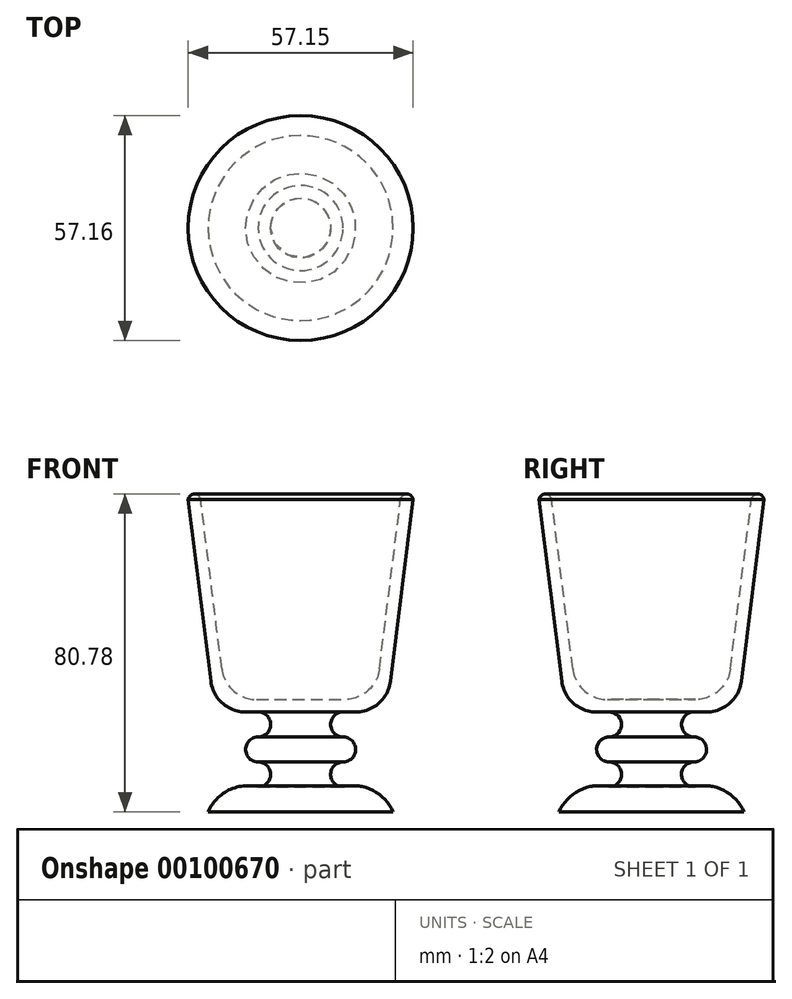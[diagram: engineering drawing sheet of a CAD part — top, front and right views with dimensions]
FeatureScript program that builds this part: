
annotation { "Feature Type Name" : "Feature", "Feature Type Description" : "" }
export const myFeature = defineFeature(function(context is Context, id is Id, definition is map)
    precondition{}
    {
        {
            var Q0;
            Q0=qCreatedBy(makeId("Front.planeOp"),FACE);
            var sketch = newSketch(context, id + "F0", { "sketchPlane" : qUnion([Q0])});
            skLineSegment(sketch, "E0", {"start": v(-10.55, -18.37) * mm, "end": v(-15.92, 24.64) * mm});
            skLineSegment(sketch, "E1", {"start": v(-19.1, 24.64) * mm, "end": v(-13.32, -21.55) * mm});
            skLineSegment(sketch, "E2", {"start": v(-4.5, -29.34) * mm, "end": v(-1.32, -29.34) * mm});
            skArc(sketch, "E3", {"start": v(-1.32, -35.69) * mm, "mid": v(1.86, -32.51) * mm, "end": v(-1.32, -29.34) * mm});
            skArc(sketch, "E4", {"start": v(-1.32, -35.69) * mm, "mid": v(-4.5, -38.86) * mm, "end": v(-1.32, -42.04) * mm});
            skLineSegment(sketch, "E5", {"start": v(-1.72, -26.16) * mm, "end": v(9.48, -26.16) * mm});
            skArc(sketch, "E6", {"start": v(-1.32, -48.39) * mm, "mid": v(1.87, -45.21) * mm, "end": v(-1.32, -42.04) * mm});
            skArc(sketch, "E7", {"start": v(-1.32, -48.39) * mm, "mid": v(-8.84, -49.22) * mm, "end": v(-14.02, -54.74) * mm});
            skPoint(sketch, "E8.visualSharp", {"position": v(-9.57, -26.16) * mm});
            skArc(sketch, "E8.filletArc", {"start": v(-10.55, -18.37) * mm, "mid": v(-7.6, -23.94) * mm, "end": v(-1.72, -26.16) * mm});
            skPoint(sketch, "E9.visualSharp", {"position": v(-12.35, -29.34) * mm});
            skArc(sketch, "E9.filletArc", {"start": v(-13.32, -21.55) * mm, "mid": v(-10.39, -27.11) * mm, "end": v(-4.5, -29.34) * mm});
            skArc(sketch, "E10", {"start": v(-15.92, 24.64) * mm, "mid": v(-17.5, 26.04) * mm, "end": v(-19.1, 24.64) * mm});
            skLineSegment(sketch, "E11", {"start": v(9.48, -54.74) * mm, "end": v(-14.02, -54.74) * mm});
            skLineSegment(sketch, "E12", {"start": v(9.48, -26.16) * mm, "end": v(9.48, -54.74) * mm});
            skLineSegment(sketch, "E13", {"start": v(9.48, -26.16) * mm, "end": v(9.48, 6.73) * mm, "construction": true});
            skSolve(sketch);
        }
        {
            var Q0;
            Q0=makeQuery(id+"F0.imprint","IMPRINT",FACE,{"disambiguationData":[TD([[makeQuery(id+"F0.imprint","IMPRINT",EDGE,{"derivedFrom":sQuery(id+"F0.wireOp",EDGE,"E0")}),1.0]])]});
            var Q1;
            Q1=sQuery(id+"F0.wireOp",EDGE,"E13");
            revolve(context, id + "F1", {"entities" : qUnion([Q0]), "axis" : qUnion([Q1]), "revolveType" : RevolveType.FULL});
        }
    });
